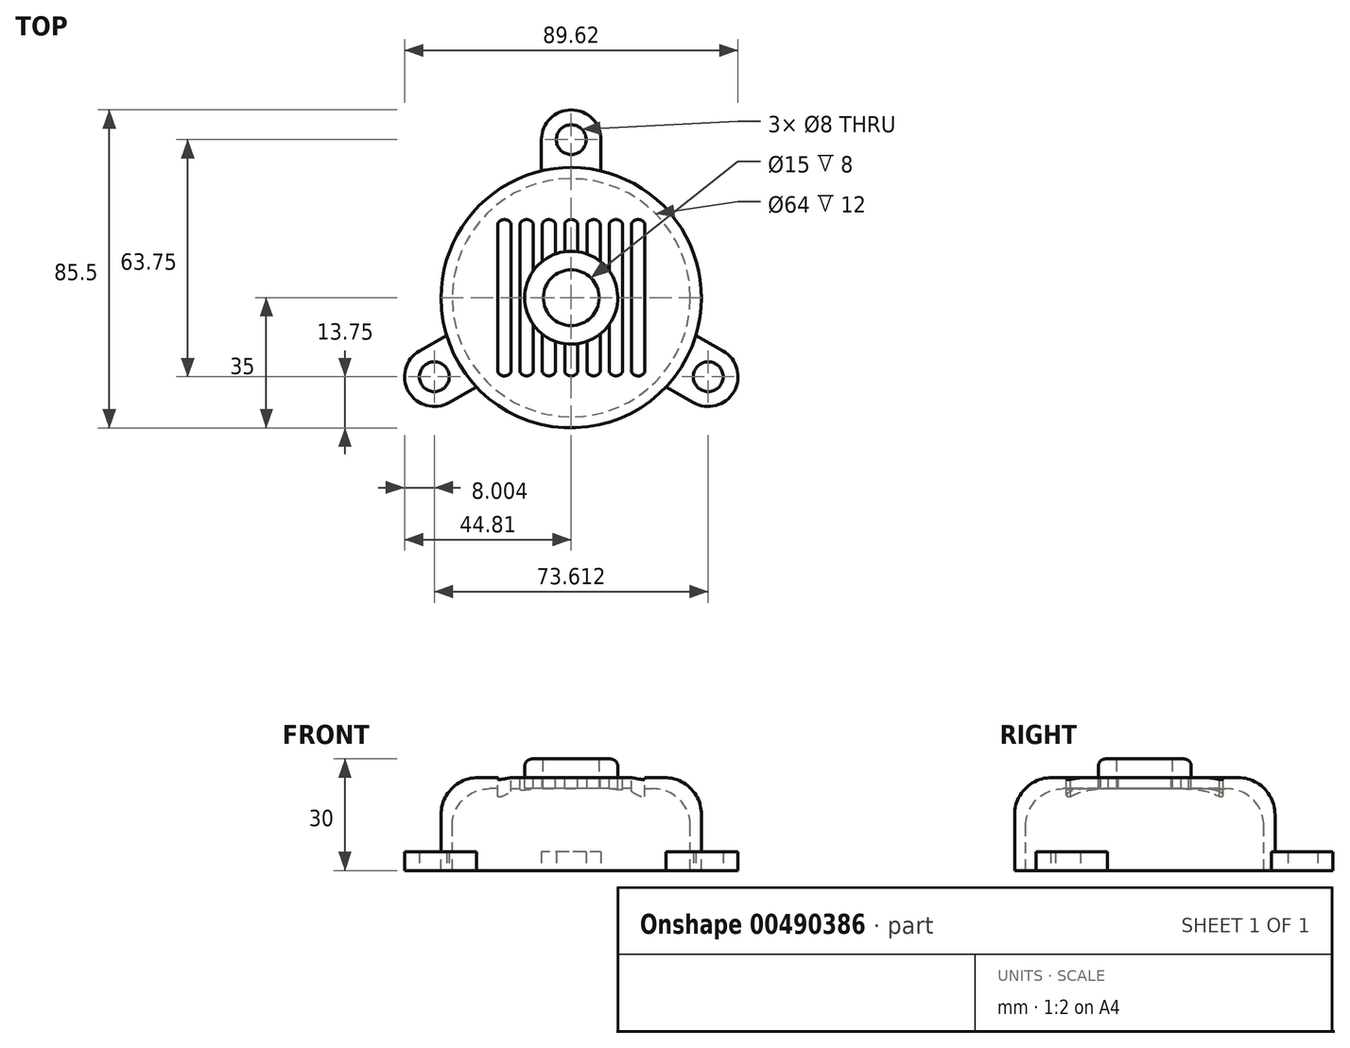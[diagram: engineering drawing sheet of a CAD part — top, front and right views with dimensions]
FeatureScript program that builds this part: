
annotation { "Feature Type Name" : "Feature", "Feature Type Description" : "" }
export const myFeature = defineFeature(function(context is Context, id is Id, definition is map)
    precondition{}
    {
        {
            var Q0;
            Q0=qCreatedBy(makeId("Front.planeOp"),FACE);
            var sketch = newSketch(context, id + "F0", { "sketchPlane" : qUnion([Q0])});
            skLineSegment(sketch, "E0", {"start": v(7.5, 30) * mm, "end": v(7.5, 22) * mm});
            skLineSegment(sketch, "E1", {"start": v(7.5, 22) * mm, "end": v(32, 22) * mm});
            skLineSegment(sketch, "E2", {"start": v(32, 22) * mm, "end": v(32, 0) * mm});
            skLineSegment(sketch, "E3", {"start": v(32, 0) * mm, "end": v(35, 0) * mm});
            skLineSegment(sketch, "E4", {"start": v(35, 0) * mm, "end": v(35, 25) * mm});
            skLineSegment(sketch, "E5", {"start": v(35, 25) * mm, "end": v(12.5, 25) * mm});
            skLineSegment(sketch, "E6", {"start": v(12.5, 25) * mm, "end": v(12.5, 30) * mm});
            skLineSegment(sketch, "E7", {"start": v(12.5, 30) * mm, "end": v(7.5, 30) * mm});
            skLineSegment(sketch, "E8", {"start": v(0, 37.16) * mm, "end": v(0, -5.37) * mm, "construction": true});
            skSolve(sketch);
        }
        {
            var Q0;
            Q0=makeQuery(id+"F0.imprint","IMPRINT",FACE,{"disambiguationData":[TD([[makeQuery(id+"F0.imprint","IMPRINT",EDGE,{"derivedFrom":sQuery(id+"F0.wireOp",EDGE,"E0")}),1.0]])]});
            var Q1;
            Q1=sQuery(id+"F0.wireOp",EDGE,"E8");
            revolve(context, id + "F1", {"entities" : qUnion([Q0]), "axis" : qUnion([Q1]), "revolveType" : RevolveType.FULL});
        }
        {
            var Q0;
            Q0=qCreatedBy(makeId("Top.planeOp"),FACE);
            var sketch = newSketch(context, id + "F2", { "sketchPlane" : qUnion([Q0])});
            skCircle(sketch, "E9", {"center": v(0, 42.5) * mm, "radius": 4 * mm});
            skArc(sketch, "E10", {"start": v(8, 42.5) * mm, "mid": v(0, 50.5) * mm, "end": v(-8, 42.5) * mm});
            skArc(sketch, "E11.0", {"start": v(8, 34.07) * mm, "mid": v(0, 35) * mm, "end": v(-8, 34.07) * mm});
            skLineSegment(sketch, "E12", {"start": v(8, 42.5) * mm, "end": v(8, 34.07) * mm});
            skLineSegment(sketch, "E13", {"start": v(-8, 42.5) * mm, "end": v(-8, 34.07) * mm});
            skLineSegment(sketch, "E14.1.0", {"start": v(32.8, -28.18) * mm, "end": v(25.5, -23.96) * mm});
            skArc(sketch, "E14.1.1", {"start": v(25.5, -23.96) * mm, "mid": v(30.31, -17.5) * mm, "end": v(33.5, -10.1) * mm});
            skLineSegment(sketch, "E14.1.2", {"start": v(40.8, -14.32) * mm, "end": v(33.5, -10.1) * mm});
            skArc(sketch, "E14.1.3", {"start": v(32.8, -28.18) * mm, "mid": v(43.73, -25.25) * mm, "end": v(40.8, -14.32) * mm});
            skCircle(sketch, "E14.1.4", {"center": v(36.8, -21.25) * mm, "radius": 4 * mm});
            skLineSegment(sketch, "E14.2.0", {"start": v(-40.8, -14.32) * mm, "end": v(-33.5, -10.1) * mm});
            skArc(sketch, "E14.2.1", {"start": v(-33.5, -10.1) * mm, "mid": v(-30.31, -17.5) * mm, "end": v(-25.5, -23.96) * mm});
            skLineSegment(sketch, "E14.2.2", {"start": v(-32.8, -28.18) * mm, "end": v(-25.5, -23.96) * mm});
            skArc(sketch, "E14.2.3", {"start": v(-40.8, -14.32) * mm, "mid": v(-43.73, -25.25) * mm, "end": v(-32.8, -28.18) * mm});
            skCircle(sketch, "E14.2.4", {"center": v(-36.8, -21.25) * mm, "radius": 4 * mm});
            skLineSegment(sketch, "E14.anchor1", {"start": v(0, 0) * mm, "end": v(0, 42.5) * mm, "construction": true});
            skLineSegment(sketch, "E14.anchor2", {"start": v(0, 0) * mm, "end": v(-36.8, -21.25) * mm, "construction": true});
            skSolve(sketch);
        }
        {
            var Q0;
            Q0 = qSketchRegion(id + "F2", true);
            extrude(context, id + "F3", {"entities" : qUnion([Q0]), "operationType" : NewBodyOperationType.ADD, "depth" : 5 * mm});
        }
        {
            var Q0;
            Q0=makeQuery(id+"F1.opRevolve","SWEPT_FACE",FACE,{"disambiguationData":[OSD([sQuery(id+"F0.wireOp",EDGE,"E5")])]});
            var sketch = newSketch(context, id + "F4", { "sketchPlane" : qUnion([Q0])});
            skLineSegment(sketch, "E15", {"start": v(0, 32.56) * mm, "end": v(0, 12.5) * mm, "construction": true});
            skLineSegment(sketch, "E16", {"start": v(1.75, 20) * mm, "end": v(1.75, 12.38) * mm});
            skLineSegment(sketch, "E17", {"start": v(-1.75, -20) * mm, "end": v(-1.75, -12.38) * mm});
            skArc(sketch, "E18", {"start": v(1.75, 20) * mm, "mid": v(0, 21.03) * mm, "end": v(-1.75, 20) * mm});
            skArc(sketch, "E19", {"start": v(-1.75, -20) * mm, "mid": v(0, -21.03) * mm, "end": v(1.75, -20) * mm});
            skLineSegment(sketch, "E20", {"start": v(-4.38, 0) * mm, "end": v(4, 0) * mm, "construction": true});
            skLineSegment(sketch, "E21.1.0.0", {"start": v(7.75, 20) * mm, "end": v(7.75, 9.8) * mm});
            skLineSegment(sketch, "E21.1.0.1", {"start": v(6, 32.56) * mm, "end": v(6, 10.97) * mm, "construction": true});
            skLineSegment(sketch, "E21.1.0.2", {"start": v(4.25, -20) * mm, "end": v(4.25, -11.76) * mm});
            skArc(sketch, "E21.1.0.3", {"start": v(7.75, 20) * mm, "mid": v(6, 21.03) * mm, "end": v(4.25, 20) * mm});
            skLineSegment(sketch, "E21.1.0.4", {"start": v(1.62, 0) * mm, "end": v(10, 0) * mm, "construction": true});
            skArc(sketch, "E21.1.0.5", {"start": v(4.25, -20) * mm, "mid": v(6, -21.03) * mm, "end": v(7.75, -20) * mm});
            skLineSegment(sketch, "E21.2.0.0", {"start": v(13.75, 20) * mm, "end": v(13.75, -20) * mm});
            skLineSegment(sketch, "E21.2.0.1", {"start": v(12, 32.56) * mm, "end": v(12, -33.71) * mm, "construction": true});
            skLineSegment(sketch, "E21.2.0.2", {"start": v(10.25, -20) * mm, "end": v(10.25, -7.15) * mm});
            skArc(sketch, "E21.2.0.3", {"start": v(13.75, 20) * mm, "mid": v(12, 21.03) * mm, "end": v(10.25, 20) * mm});
            skLineSegment(sketch, "E21.2.0.4", {"start": v(7.62, 0) * mm, "end": v(16, 0) * mm, "construction": true});
            skArc(sketch, "E21.2.0.5", {"start": v(10.25, -20) * mm, "mid": v(12, -21.03) * mm, "end": v(13.75, -20) * mm});
            skLineSegment(sketch, "E21.3.0.0", {"start": v(19.75, 20) * mm, "end": v(19.75, -20) * mm});
            skLineSegment(sketch, "E21.3.0.1", {"start": v(18, 32.56) * mm, "end": v(18, -33.71) * mm, "construction": true});
            skLineSegment(sketch, "E21.3.0.2", {"start": v(16.25, -20) * mm, "end": v(16.25, 20) * mm});
            skArc(sketch, "E21.3.0.3", {"start": v(19.75, 20) * mm, "mid": v(18, 21.03) * mm, "end": v(16.25, 20) * mm});
            skLineSegment(sketch, "E21.3.0.4", {"start": v(13.62, 0) * mm, "end": v(22, 0) * mm, "construction": true});
            skArc(sketch, "E21.3.0.5", {"start": v(16.25, -20) * mm, "mid": v(18, -21.03) * mm, "end": v(19.75, -20) * mm});
            skLineSegment(sketch, "E21.direction1", {"start": v(1.75, -20) * mm, "end": v(7.75, -20) * mm, "construction": true});
            skLineSegment(sketch, "E22.1.0.0", {"start": v(-6, 32.56) * mm, "end": v(-6, 10.97) * mm, "construction": true});
            skLineSegment(sketch, "E22.1.0.1", {"start": v(-7.75, -20) * mm, "end": v(-7.75, -9.8) * mm});
            skLineSegment(sketch, "E22.1.0.2", {"start": v(-4.25, 20) * mm, "end": v(-4.25, 11.76) * mm});
            skArc(sketch, "E22.1.0.3", {"start": v(-4.25, 20) * mm, "mid": v(-6, 21.03) * mm, "end": v(-7.75, 20) * mm});
            skLineSegment(sketch, "E22.1.0.4", {"start": v(-10.38, 0) * mm, "end": v(-2, 0) * mm, "construction": true});
            skArc(sketch, "E22.1.0.5", {"start": v(-7.75, -20) * mm, "mid": v(-6, -21.03) * mm, "end": v(-4.25, -20) * mm});
            skLineSegment(sketch, "E22.2.0.0", {"start": v(-12, 32.56) * mm, "end": v(-12, 3.5) * mm, "construction": true});
            skLineSegment(sketch, "E22.2.0.1", {"start": v(-13.75, -20) * mm, "end": v(-13.75, 20) * mm});
            skLineSegment(sketch, "E22.2.0.2", {"start": v(-10.25, 20) * mm, "end": v(-10.25, 7.15) * mm});
            skArc(sketch, "E22.2.0.3", {"start": v(-10.25, 20) * mm, "mid": v(-12, 21.03) * mm, "end": v(-13.75, 20) * mm});
            skLineSegment(sketch, "E22.2.0.4", {"start": v(-16.38, 0) * mm, "end": v(-8, 0) * mm, "construction": true});
            skArc(sketch, "E22.2.0.5", {"start": v(-13.75, -20) * mm, "mid": v(-12, -21.03) * mm, "end": v(-10.25, -20) * mm});
            skLineSegment(sketch, "E22.3.0.0", {"start": v(-18, 32.56) * mm, "end": v(-18, -33.71) * mm, "construction": true});
            skLineSegment(sketch, "E22.3.0.1", {"start": v(-19.75, -20) * mm, "end": v(-19.75, 20) * mm});
            skLineSegment(sketch, "E22.3.0.2", {"start": v(-16.25, 20) * mm, "end": v(-16.25, -20) * mm});
            skArc(sketch, "E22.3.0.3", {"start": v(-16.25, 20) * mm, "mid": v(-18, 21.03) * mm, "end": v(-19.75, 20) * mm});
            skLineSegment(sketch, "E22.3.0.4", {"start": v(-22.38, 0) * mm, "end": v(-14, 0) * mm, "construction": true});
            skArc(sketch, "E22.3.0.5", {"start": v(-19.75, -20) * mm, "mid": v(-18, -21.03) * mm, "end": v(-16.25, -20) * mm});
            skLineSegment(sketch, "E22.direction1", {"start": v(0, -33.71) * mm, "end": v(-6, -33.71) * mm, "construction": true});
            skArc(sketch, "E23.0", {"start": v(-10.25, 7.15) * mm, "mid": v(-12.5, 0) * mm, "end": v(-10.25, -7.15) * mm});
            skLineSegment(sketch, "E24.trimOffspring", {"start": v(4.25, 11.76) * mm, "end": v(4.25, 20) * mm});
            skLineSegment(sketch, "E25.trimOffspring", {"start": v(1.75, -12.38) * mm, "end": v(1.75, -20) * mm});
            skLineSegment(sketch, "E26.trimOffspring", {"start": v(-1.75, 12.38) * mm, "end": v(-1.75, 20) * mm});
            skLineSegment(sketch, "E27.trimOffspring", {"start": v(-4.25, -11.76) * mm, "end": v(-4.25, -20) * mm});
            skLineSegment(sketch, "E28.trimOffspring", {"start": v(-7.75, 9.8) * mm, "end": v(-7.75, 20) * mm});
            skLineSegment(sketch, "E29.trimOffspring", {"start": v(-10.25, -7.15) * mm, "end": v(-10.25, -20) * mm});
            skLineSegment(sketch, "E30.trimOffspring", {"start": v(7.75, -9.8) * mm, "end": v(7.75, -20) * mm});
            skLineSegment(sketch, "E31.trimOffspring", {"start": v(10.25, 7.15) * mm, "end": v(10.25, 20) * mm});
            skLineSegment(sketch, "E32.trimOffspring", {"start": v(0, -12.5) * mm, "end": v(0, -33.71) * mm, "construction": true});
            skLineSegment(sketch, "E33.trimOffspring", {"start": v(6, -10.97) * mm, "end": v(6, -33.71) * mm, "construction": true});
            skLineSegment(sketch, "E34.trimOffspring", {"start": v(-6, -10.97) * mm, "end": v(-6, -33.71) * mm, "construction": true});
            skLineSegment(sketch, "E35.trimOffspring", {"start": v(-12, -3.5) * mm, "end": v(-12, -33.71) * mm, "construction": true});
            skArc(sketch, "E36.trimOffspring", {"start": v(-4.25, 11.76) * mm, "mid": v(-6.08, 10.92) * mm, "end": v(-7.75, 9.8) * mm});
            skArc(sketch, "E37.trimOffspring", {"start": v(1.75, 12.38) * mm, "mid": v(0, 12.5) * mm, "end": v(-1.75, 12.38) * mm});
            skArc(sketch, "E38.trimOffspring", {"start": v(7.75, 9.8) * mm, "mid": v(6.08, 10.92) * mm, "end": v(4.25, 11.76) * mm});
            skArc(sketch, "E39.trimOffspring", {"start": v(10.25, -7.15) * mm, "mid": v(12.5, 0) * mm, "end": v(10.25, 7.15) * mm});
            skArc(sketch, "E40.trimOffspring", {"start": v(4.25, -11.76) * mm, "mid": v(6.08, -10.92) * mm, "end": v(7.75, -9.8) * mm});
            skArc(sketch, "E41.trimOffspring", {"start": v(-1.75, -12.38) * mm, "mid": v(0, -12.5) * mm, "end": v(1.75, -12.38) * mm});
            skArc(sketch, "E42.trimOffspring", {"start": v(-7.75, -9.8) * mm, "mid": v(-6.08, -10.92) * mm, "end": v(-4.25, -11.76) * mm});
            skSolve(sketch);
        }
        {
            var Q0;
            Q0 = qSketchRegion(id + "F4", true);
            extrude(context, id + "F5", {"entities" : qUnion([Q0]), "operationType" : NewBodyOperationType.REMOVE, "endBound" : BoundingType.UP_TO_NEXT, "oppositeDirection" : true, "depth" : 25 * mm});
        }
        {
            var Q0;
            Q0=makeQuery(id+"F1.opRevolve","SWEPT_EDGE",EDGE,{"disambiguationData":[OSD([sQuery(id+"F0.wireOp",EDGE,"E6"),sQuery(id+"F0.wireOp",EDGE,"E7")])]});
            fillet(context, id + "F6", {"entities" : qUnion([Q0]), "radius" : 2 * mm, "allowEdgeOverflow" : false});
        }
        {
            var Q0;
            Q0=makeQuery(id+"F1.opRevolve","SWEPT_EDGE",EDGE,{"disambiguationData":[OSD([sQuery(id+"F0.wireOp",EDGE,"E1"),sQuery(id+"F0.wireOp",EDGE,"E2")])]});
            fillet(context, id + "F7", {"entities" : qUnion([Q0]), "radius" : 10 * mm, "tangentPropagation" : true, "allowEdgeOverflow" : false});
        }
        {
            var Q0;
            Q0=makeQuery(id+"F1.opRevolve","SWEPT_EDGE",EDGE,{"disambiguationData":[OSD([sQuery(id+"F0.wireOp",EDGE,"E4"),sQuery(id+"F0.wireOp",EDGE,"E5")])]});
            fillet(context, id + "F8", {"entities" : qUnion([Q0]), "radius" : 10 * mm, "allowEdgeOverflow" : false});
        }
    });
